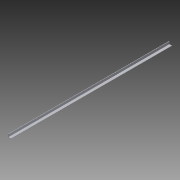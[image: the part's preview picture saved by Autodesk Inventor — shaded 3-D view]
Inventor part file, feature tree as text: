
AUTODESK INVENTOR PART (.ipt)
format: ipt  version: 2014 SP1 (Build 180222100, 222)  size: 74,752 bytes
history: native  units: in
note: dims shown in document units (in); Inventor stores cm internally (conversion verified against a paired STEP export)
features: extrude x1, sketch x1
ambient origin geometry x8: Origin, YZ Plane, XZ Plane, XY Plane, X Axis, Y Axis, Z Axis, Center Point
bodies: Solid1 (feature_tree)
feature tree (2):
  extrude  "Extrusion1"  Depth=0.0625in
  sketch  "Sketch1"  dims[d0=0.5in d1=0.0625in d2=0.5in d3=0.0625in d4=27.25in d5=0.0in]
